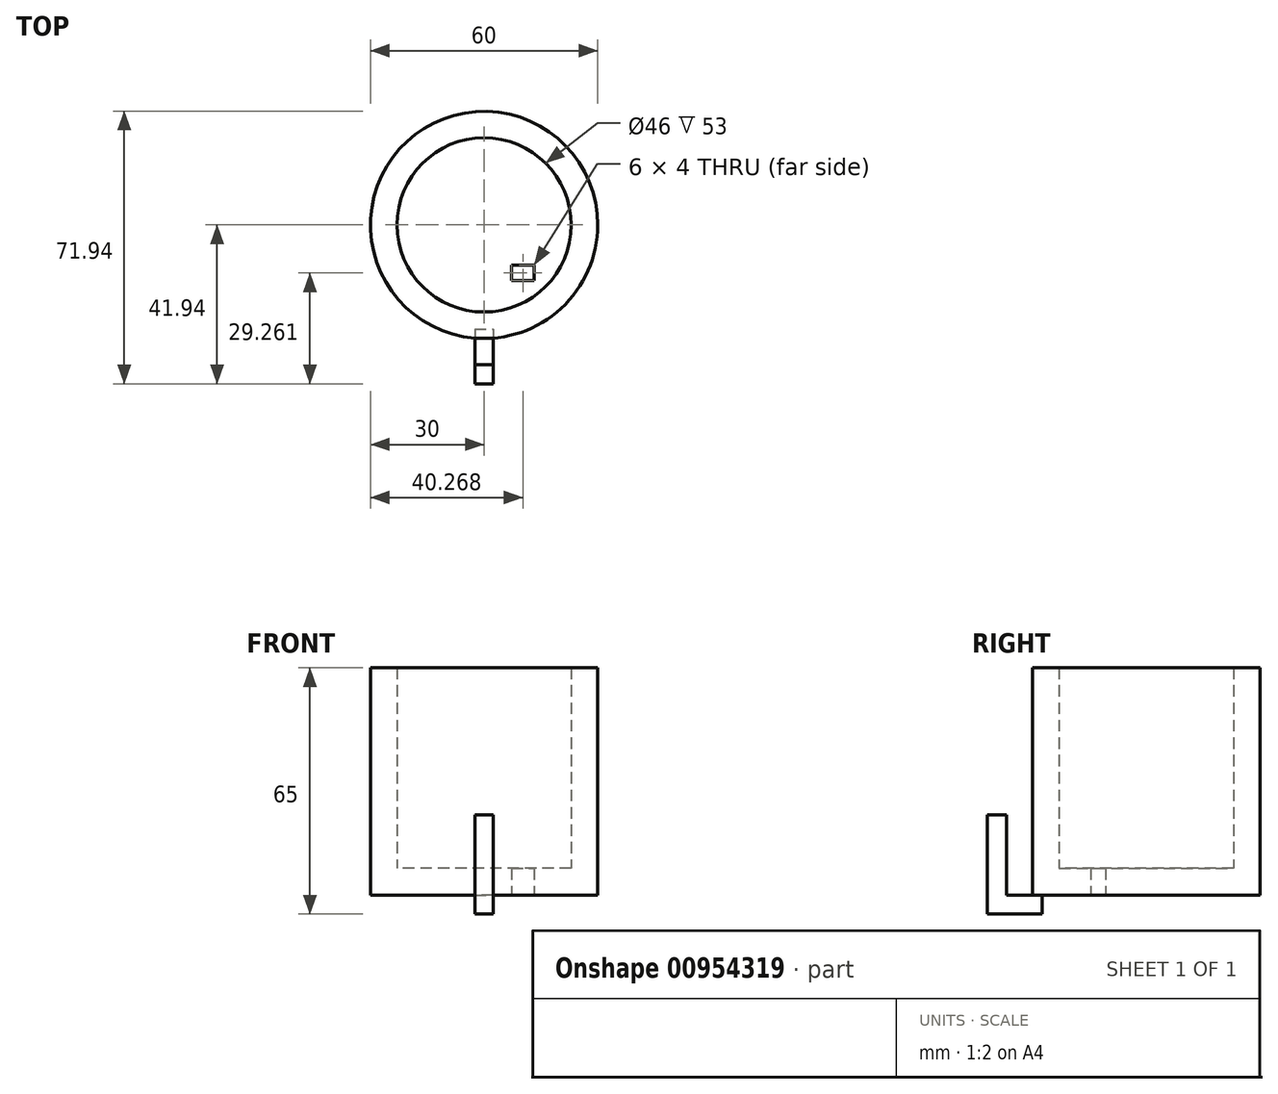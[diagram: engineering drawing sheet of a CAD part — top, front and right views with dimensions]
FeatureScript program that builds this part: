
annotation { "Feature Type Name" : "Feature", "Feature Type Description" : "" }
export const myFeature = defineFeature(function(context is Context, id is Id, definition is map)
    precondition{}
    {
        {
            var Q0;
            Q0=qCreatedBy(makeId("Top.planeOp"),FACE);
            var sketch = newSketch(context, id + "F0", { "sketchPlane" : qUnion([Q0])});
            skCircle(sketch, "E0", {"center": v(0, 0) * mm, "radius": 30 * mm});
            skSolve(sketch);
        }
        {
            var Q0;
            Q0=makeQuery(id+"F0.imprint","IMPRINT",FACE,{"disambiguationData":[TD([[makeQuery(id+"F0.imprint","IMPRINT",EDGE,{"derivedFrom":sQuery(id+"F0.wireOp",EDGE,"E0")}),1.0]])]});
            extrude(context, id + "F1", {"entities" : qUnion([Q0]), "depth" : 60 * mm, "offsetDistance" : 25 * mm});
        }
        {
            var Q0;
            Q0=makeQuery(id+"F1.opExtrude","CAP_FACE",FACE,{"disambiguationData":[OSD([sQuery(id+"F0.wireOp",EDGE,"E0")])],"isStart":false});
            shell(context, id + "F2", {"entities" : qUnion([Q0]), "thickness" : 7 * mm});
        }
        {
            var Q0;
            Q0=makeQuery(id+"F1.opExtrude","CAP_FACE",FACE,{"disambiguationData":[OSD([sQuery(id+"F0.wireOp",EDGE,"E0")])],"isStart":true});
            var sketch = newSketch(context, id + "F3", { "sketchPlane" : qUnion([Q0])});
            skLineSegment(sketch, "E1.bottom", {"start": v(7.27, 14.68) * mm, "end": v(13.27, 14.68) * mm});
            skLineSegment(sketch, "E1.top", {"start": v(7.27, 10.68) * mm, "end": v(13.27, 10.68) * mm});
            skLineSegment(sketch, "E1.left", {"start": v(7.27, 14.68) * mm, "end": v(7.27, 10.68) * mm});
            skLineSegment(sketch, "E1.right", {"start": v(13.27, 14.68) * mm, "end": v(13.27, 10.68) * mm});
            skSolve(sketch);
        }
        {
            var Q0;
            Q0=makeQuery(id+"F3.imprint","IMPRINT",FACE,{"disambiguationData":[TD([[makeQuery(id+"F3.imprint","IMPRINT",EDGE,{"derivedFrom":sQuery(id+"F3.wireOp",EDGE,"E1.bottom")}),-1.0]])]});
            extrude(context, id + "F4", {"entities" : qUnion([Q0]), "operationType" : NewBodyOperationType.REMOVE, "oppositeDirection" : true, "depth" : 7 * mm, "offsetDistance" : 25 * mm});
        }
        {
            var Q0;
            Q0=makeQuery(id+"F1.opExtrude","CAP_FACE",FACE,{"disambiguationData":[OSD([sQuery(id+"F0.wireOp",EDGE,"E0")])],"isStart":true});
            var sketch = newSketch(context, id + "F5", { "sketchPlane" : qUnion([Q0])});
            skLineSegment(sketch, "E2.bottom", {"start": v(-2.47, 27.48) * mm, "end": v(2.41, 27.48) * mm});
            skLineSegment(sketch, "E2.top", {"start": v(-2.47, 36.94) * mm, "end": v(2.41, 36.94) * mm});
            skLineSegment(sketch, "E2.left", {"start": v(-2.47, 27.48) * mm, "end": v(-2.47, 36.94) * mm});
            skLineSegment(sketch, "E2.right", {"start": v(2.41, 27.48) * mm, "end": v(2.41, 36.94) * mm});
            skSolve(sketch);
        }
        {
            var Q0;
            {var subQ0=sQuery(id+"F5.wireOp",EDGE,"E2.top");Q0=makeQuery(id+"F5.imprint","IMPRINT",FACE,{"disambiguationData":[TD([[makeQuery(id+"F5.imprint","IMPRINT",EDGE,{"derivedFrom":subQ0}),-1.0]])]});}
            var Q1;
            {var subQ0=sQuery(id+"F5.wireOp",EDGE,"E2.bottom");Q1=makeQuery(id+"F5.imprint","IMPRINT",FACE,{"disambiguationData":[TD([[makeQuery(id+"F5.imprint","IMPRINT",EDGE,{"derivedFrom":subQ0}),1.0]])]});}
            extrude(context, id + "F6", {"entities" : qUnion([Q0, Q1]), "operationType" : NewBodyOperationType.ADD, "depth" : 5 * mm, "offsetDistance" : 25 * mm});
        }
        {
            var Q0;
            Q0=makeQuery(id+"F6.opExtrude","SWEPT_FACE",FACE,{"disambiguationData":[OSD([sQuery(id+"F5.wireOp",EDGE,"E2.top")])]});
            var sketch = newSketch(context, id + "F7", { "sketchPlane" : qUnion([Q0])});
            skLineSegment(sketch, "E3.bottom", {"start": v(-2.47, -5) * mm, "end": v(2.41, -5) * mm});
            skLineSegment(sketch, "E3.top", {"start": v(-2.47, 21.13) * mm, "end": v(2.41, 21.13) * mm});
            skLineSegment(sketch, "E3.left", {"start": v(-2.47, -5) * mm, "end": v(-2.47, 21.13) * mm});
            skLineSegment(sketch, "E3.right", {"start": v(2.41, -5) * mm, "end": v(2.41, 21.13) * mm});
            skSolve(sketch);
        }
        {
            var Q0;
            {var subQ0=sQuery(id+"F7.wireOp",EDGE,"E3.top");Q0=makeQuery(id+"F7.imprint","IMPRINT",FACE,{"disambiguationData":[TD([[makeQuery(id+"F7.imprint","IMPRINT",EDGE,{"derivedFrom":subQ0}),-1.0]])]});}
            var Q1;
            {var subQ0=sQuery(id+"F7.wireOp",EDGE,"E3.bottom");Q1=makeQuery(id+"F7.imprint","IMPRINT",FACE,{"disambiguationData":[TD([[makeQuery(id+"F7.imprint","IMPRINT",EDGE,{"derivedFrom":subQ0}),1.0]])]});}
            extrude(context, id + "F8", {"entities" : qUnion([Q0, Q1]), "operationType" : NewBodyOperationType.ADD, "depth" : 5 * mm, "offsetDistance" : 25 * mm});
        }
    });
